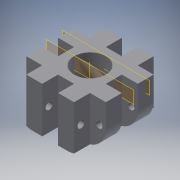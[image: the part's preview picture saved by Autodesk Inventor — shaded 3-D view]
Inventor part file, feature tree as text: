
AUTODESK INVENTOR PART (.ipt)
format: ipt  version: 2018 (Build 220112000, 112)  size: 267,264 bytes
history: native  units: mm
features: sketch x4, extrude x3, plane x2, fillet x2, pattern_circular x1, other x1, helix x1
ambient origin geometry x8: Origin, YZ Plane, XZ Plane, XY Plane, X Axis, Y Axis, Z Axis, Center Point
bodies: Solid1 (feature_tree)
feature tree (14):
  extrude  "Extrusion1"  Depth=20.0mm
  extrude  "Extrusion6"  Depth=7.0mm
  extrude  "Extrusion7"  Depth=7.0mm
  pattern_circular  "Circular Pattern3"  [2 undecoded]
  plane  "Work Plane3"
  sketch  "Sketch10"  dims[d59=7.0mm d60=7.0mm d61=7.0mm d62=90.0deg d63=7.0mm d64=7.0mm d65=90.0deg d66=7.0mm d67=7.0mm d68=7.0mm d69=7.0mm d70=7.0mm d71=7.0mm d72=7.0mm d73=7.0mm d74=7.0mm d75=7.0mm d76=7.0mm d77=90.0deg d78=13.0mm d81=10.0mm d82=0.0mm d83=3.0mm d84=3.0mm d85=10.0mm d86=0.0mm d87=40.0mm d88=360.0deg d93=7.0mm d94=14.0mm d95=7.0mm d100=2.5mm d101=5.0mm d102=35.0mm d103=15.0mm d104=10.0mm d105=0.0mm d106=90.0deg d107=90.0deg d108=0.0mm d109=0.0mm d111=2.0mm d112=10.0mm]
  other  "Work Axis1"
  helix  "Coil1"  [1 undecoded]
  fillet  "Fillet4"  [1 undecoded]
  fillet  "Fillet5"  Radius=7.0mm
  sketch  "Sketch1"  dims[d28=20.0mm d29=0.0mm d49=13.0mm]
  sketch  "Sketch6"  dims[d55=7.0mm d56=7.0mm]
  sketch  "Sketch7"  dims[d57=7.0mm d58=7.0mm]
  plane  "Work Plane2"
note: 4 required parameter values undecoded (feature->parameter linkage not recoverable at this tier; creation-order binding heuristic only, values carry confidence <= 0.55)
